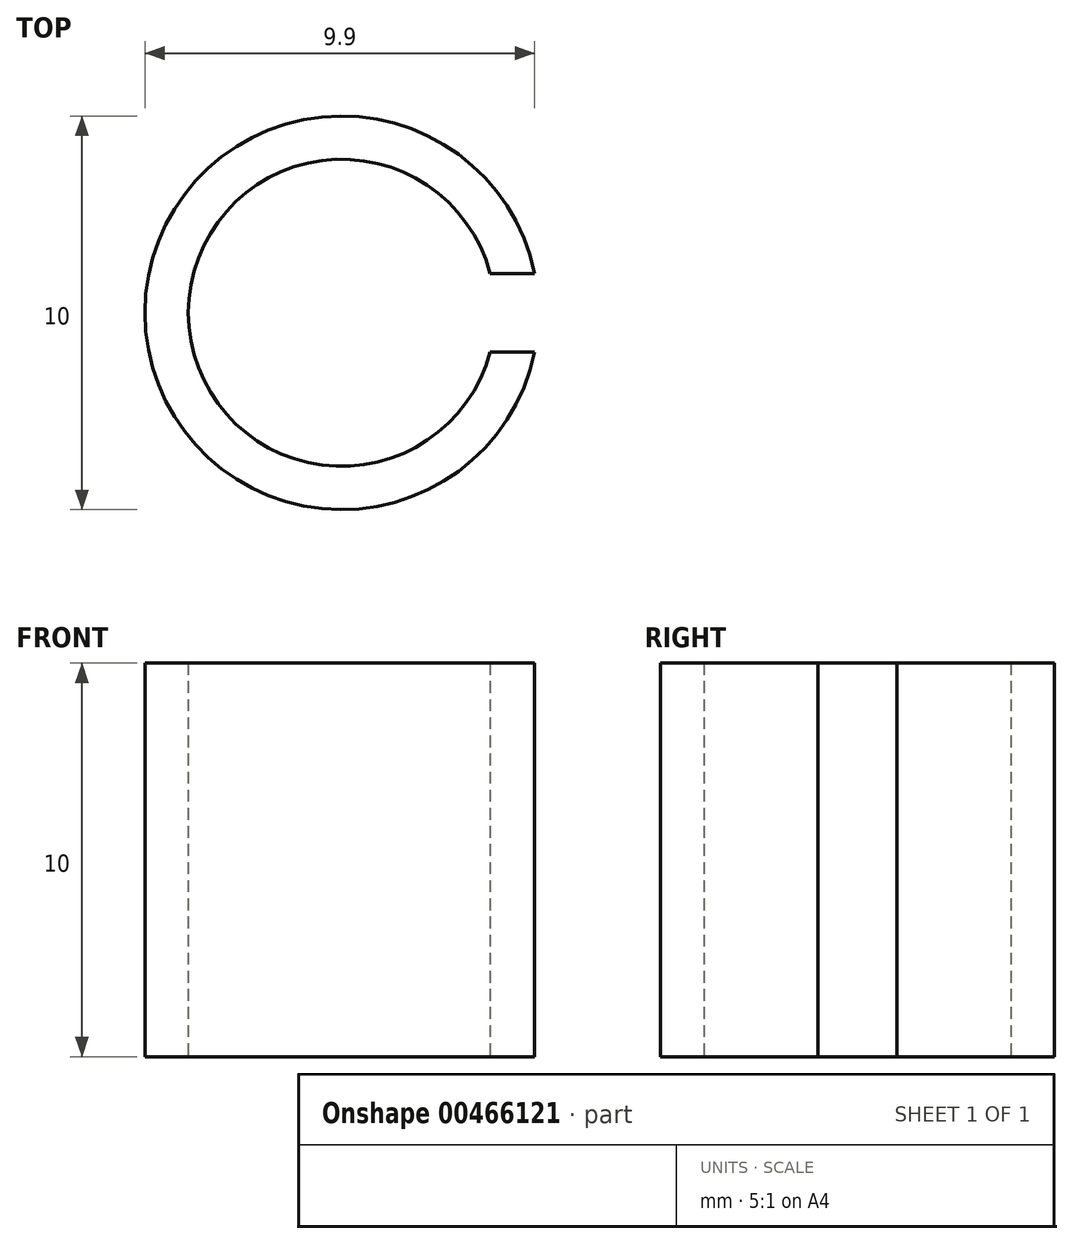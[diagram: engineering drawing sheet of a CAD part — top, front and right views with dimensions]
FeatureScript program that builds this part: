
annotation { "Feature Type Name" : "Feature", "Feature Type Description" : "" }
export const myFeature = defineFeature(function(context is Context, id is Id, definition is map)
    precondition{}
    {
        {
            var Q0;
            Q0=qCreatedBy(makeId("Top.planeOp"),FACE);
            var sketch = newSketch(context, id + "F0", { "sketchPlane" : qUnion([Q0])});
            skArc(sketch, "E0", {"start": v(3.77, 1) * mm, "mid": v(-3.9, 0) * mm, "end": v(3.77, -1) * mm});
            skArc(sketch, "E1", {"start": v(4.9, 1) * mm, "mid": v(-5, 0) * mm, "end": v(4.9, -1) * mm});
            skLineSegment(sketch, "E2", {"start": v(3.77, 1) * mm, "end": v(4.9, 1) * mm});
            skLineSegment(sketch, "E3", {"start": v(3.77, -1) * mm, "end": v(4.9, -1) * mm});
            skSolve(sketch);
        }
        {
            var Q0;
            Q0 = qSketchRegion(id + "F0", true);
            extrude(context, id + "F1", {"entities" : qUnion([Q0]), "depth" : 10 * mm});
        }
    });
